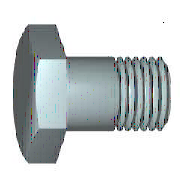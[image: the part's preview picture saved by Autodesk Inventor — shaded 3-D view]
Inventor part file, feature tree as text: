
AUTODESK INVENTOR PART (.ipt)
format: ipt  version: 2020 (Build 240168000, 168)  size: 186,880 bytes
history: native  units: mm (DEFAULTED — no unit token found)
features: sketch x3, other x1, extrude x1, chamfer x1, plane x1
ambient origin geometry x7: Origin, YZ Plane, XZ Plane, X Axis, Y Axis, Z Axis, Center Point
bodies: Solid1 (feature_tree)
feature tree (7):
  other  "轴承体"
  extrude  "头"  Depth=30.0mm
  chamfer  "倒角1"  Distance=6.9mm
  plane  "Work Plane1"
  sketch  "草图1"  dims[d0=110.0mm d1=30.0mm]
  sketch  "草图2"  dims[d2=12.0mm]
  sketch  "草图4"  dims[d12=90.0deg d3=6.9mm d4=0.0mm d5=30.0deg d21=90.0deg d6=0.920175mm d7=0.920275mm d8=0.0mm d9=0.6001mm d10=16.6mm d11=18.0mm d13=0.920275mm d14=12.0mm d15=30.0mm d16=0.0mm d19=18.0mm d55=45.0deg d57=0.0mm d58=0.0mm]
